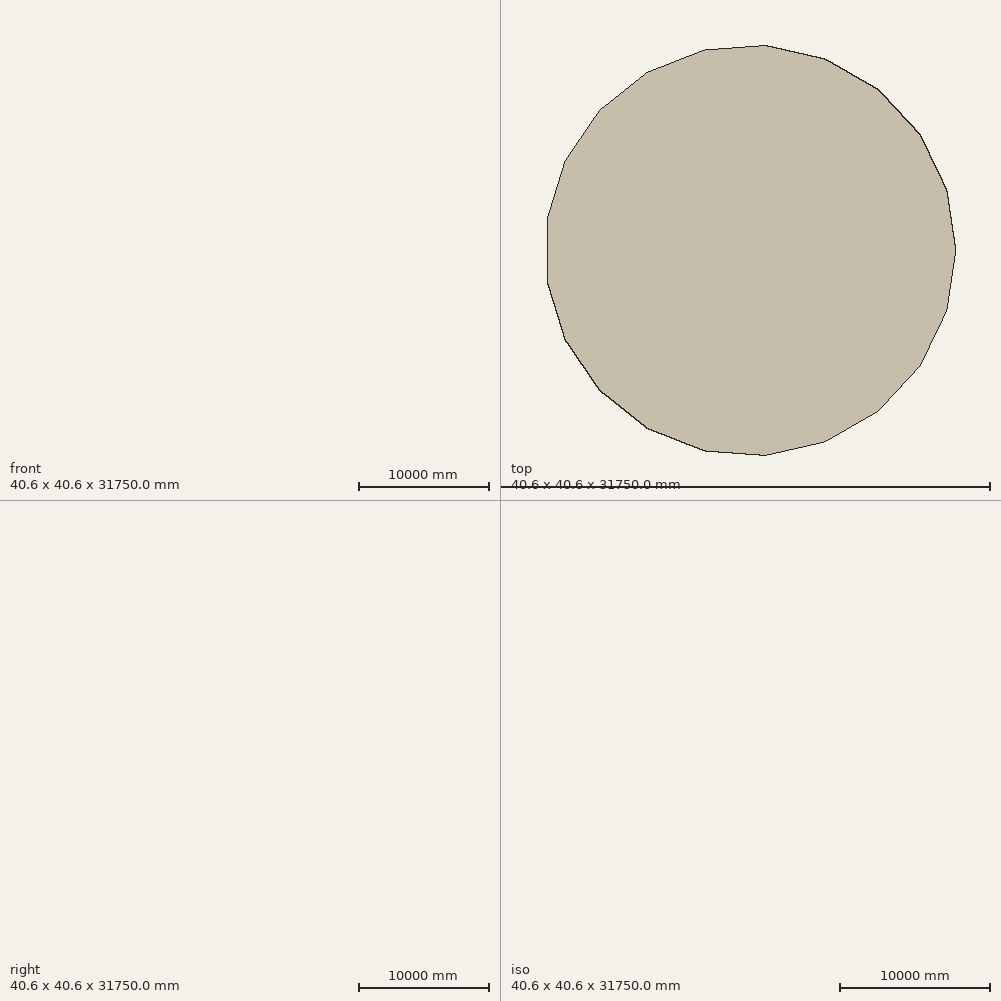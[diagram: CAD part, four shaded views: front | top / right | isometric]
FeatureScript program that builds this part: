
annotation { "Feature Type Name" : "Feature", "Feature Type Description" : "" }
export const myFeature = defineFeature(function(context is Context, id is Id, definition is map)
    precondition{}
    {
        {
            var Q0;
            Q0=qCreatedBy(makeId("Top.planeOp"),FACE);
            var sketch = newSketch(context, id + "F0", { "sketchPlane" : qUnion([Q0])});
            skCircle(sketch, "E0", {"center": v(0, 0) * mm, "radius": 20.32 * mm});
            skSolve(sketch);
        }
        {
            var Q0;
            Q0 = qSketchRegion(id + "F0", true);
            extrude(context, id + "F1", {"entities" : qUnion([Q0]), "depth" : 31750 * mm, "offsetDistance" : 25.4 * mm});
        }
    });
